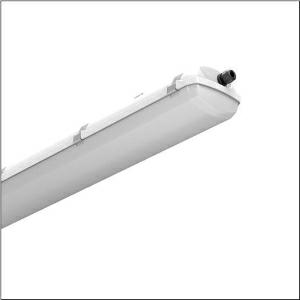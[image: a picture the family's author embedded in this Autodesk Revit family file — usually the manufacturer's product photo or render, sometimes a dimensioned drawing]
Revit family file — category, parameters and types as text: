
# Revit family: monsun_r__ex_51fxb1dp470a_532c
name_source: partatom
category: Lighting Fixtures
units: mm (PartAtom-declared; Revit-internal decimal feet)

## family parameters
Cut with Voids When Loaded = No
Host = Face
Light Source = No
Part Type = Normal
Room Calculation Point = No
Round Connector Dimension = Use Diameter
Shared = No

## types (1)
- Monsun® Ex (1 x LED, 7310 lm, 43.8 W, 4000K)
    Apparent Load = 44 VA
    CIE Flux Codes = 61 86 97 100 100
    Color Rendering = 80
    Color Temperature = 4000K
    Default Elevation = 1800 mm
    Description = Monsun® Ex, damp-proof luminaire, primary optical cover: cover, of PC, UV-stabilised, opal, light emission: direct distribution, primary light characteristic: symmetric, installation type: surface-mounted, LED, rated luminous flux: 7.310lm, luminous efficacy: 167lm/W, light colour: 840, colour temperature: 4000K, control gear: DALI 2, with terminal, 5-pole, max. 2.5mm², through-wiring: 7x 2.5mm², mains connection: 220..240V, AC, 50/60Hz, rated input power: 44W, housing, of PC, light grey (RAL 7035), incl. blind plug, incl. 1x Ex cable gland M20 for cable diameter 7..12mm with sealing, length: 1.580mm, width: 155mm, height: 105mm, clip for enclosure, of stainless steel, protection rating (complete): IP66, insulation class (complete): insulation class I (protective earthing), certification: CE, explosion class: zone2,22 II 3G Ex nR IIC T6 GC, II 3D Ex tc IIIC T80°C Dc, impact resistance: IK10, permissible operating ambient temperature: -20..+60°C, LABS conformity tested according to VDMA 24364:2018-05, contact your sales advisor before using the luminaires in applications with unclear chemical exposure, large temperature fluctuations or condensation-forming humidity, packaging unit: 1 piece
    Height = 105 mm
    Lamp = 1 x LED
    Lamp Light Flux = 7310 lm
    Lamp Power = 43.8 W
    Lamp count = 1
    Length = 1580 mm
    Luminous efficacy = 167 lm/W
    Manufacturer = Siteco
    ModVariant = No
    Model = 51FXB1DP470A
    Mounting Place = Ceiling
    Mounting Type = Surface mounted
    Number of Poles = 1
    OnlyDefault = Yes
    Power Factor = 1
    Product Name = Monsun® Ex
    Product group = damp-proof luminaire
    ProductGroupID = 300
    Protection Class = Protection class I
    Protection Degree = IP 66
    RLX_Detail_Level = 1
    RLX_Emergency_Light_Flux = 0 lm
    RLX_Emergency_Type = 0
    RLX_Emergency_Type_DB = No
    RlxData = <blob elided: 41661 chars, md5=62475180>
    Socket = socket
    Standby Power = 0 W
    System Light Flux = 7310 lm
    System Power = 44 W
    Type Comments = Product without accessories
    Type Image = l_1258882.jpg
    URL = http://relux.com
    VarID = ---
    Voltage = 0 V
    Weight = 0.00 kg
    Width = 155 mm

## geometry (parser evidence)
native form markers: Blend x4, Sweep x10
no freeform markers — native parametric forms only
